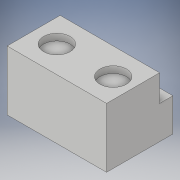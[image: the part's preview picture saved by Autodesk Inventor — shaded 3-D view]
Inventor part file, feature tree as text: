
AUTODESK INVENTOR PART (.ipt)
format: ipt  version: 2019 (Build 230136000, 136)  size: 119,296 bytes
history: native  units: mm
features: extrude x3, sketch x3, other x1
ambient origin geometry x8: Origin, YZ Plane, XZ Plane, XY Plane, X Axis, Y Axis, Z Axis, Center Point
bodies: Body1 (feature_tree)
feature tree (7):
  other  "Bryła1"
  extrude  "Wyciągnięcie proste1"  Depth=10.0mm
  extrude  "Wyciągnięcie proste2"  Depth=15.0mm
  extrude  "Wyciągnięcie proste3"  Depth=5.0mm
  sketch  "Szkic1"
  sketch  "Szkic2"
  sketch  "Szkic3"
